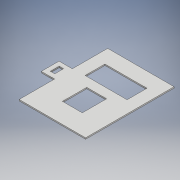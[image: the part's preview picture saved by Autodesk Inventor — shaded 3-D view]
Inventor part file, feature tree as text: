
AUTODESK INVENTOR PART (.ipt)
format: ipt  version: 2017 (Build 210142000, 142)  size: 123,904 bytes
history: native  units: mm
features: extrude x2, sketch x2
ambient origin geometry x8: Origin, YZ Plane, XZ Plane, XY Plane, X Axis, Y Axis, Z Axis, Center Point
bodies: Solid1 (feature_tree)
feature tree (4):
  extrude  "Extrusion1"  Depth=3.0mm TaperAngle=0.0deg
  extrude  "Extrusion2"  Depth=10.0mm
  sketch  "Sketch1"  dims[d0=150.0mm d23=3.0mm d24=0.0mm]
  sketch  "Sketch2"  dims[d35=10.0mm d45=10.0mm d47=3.0mm d48=0.0mm d49=200.0mm d50=40.0mm d51=80.0mm d52=10.0mm d53=95.0mm d54=45.0mm d55=45.0mm d56=55.0mm d41=10.0mm d42=10.0mm]
